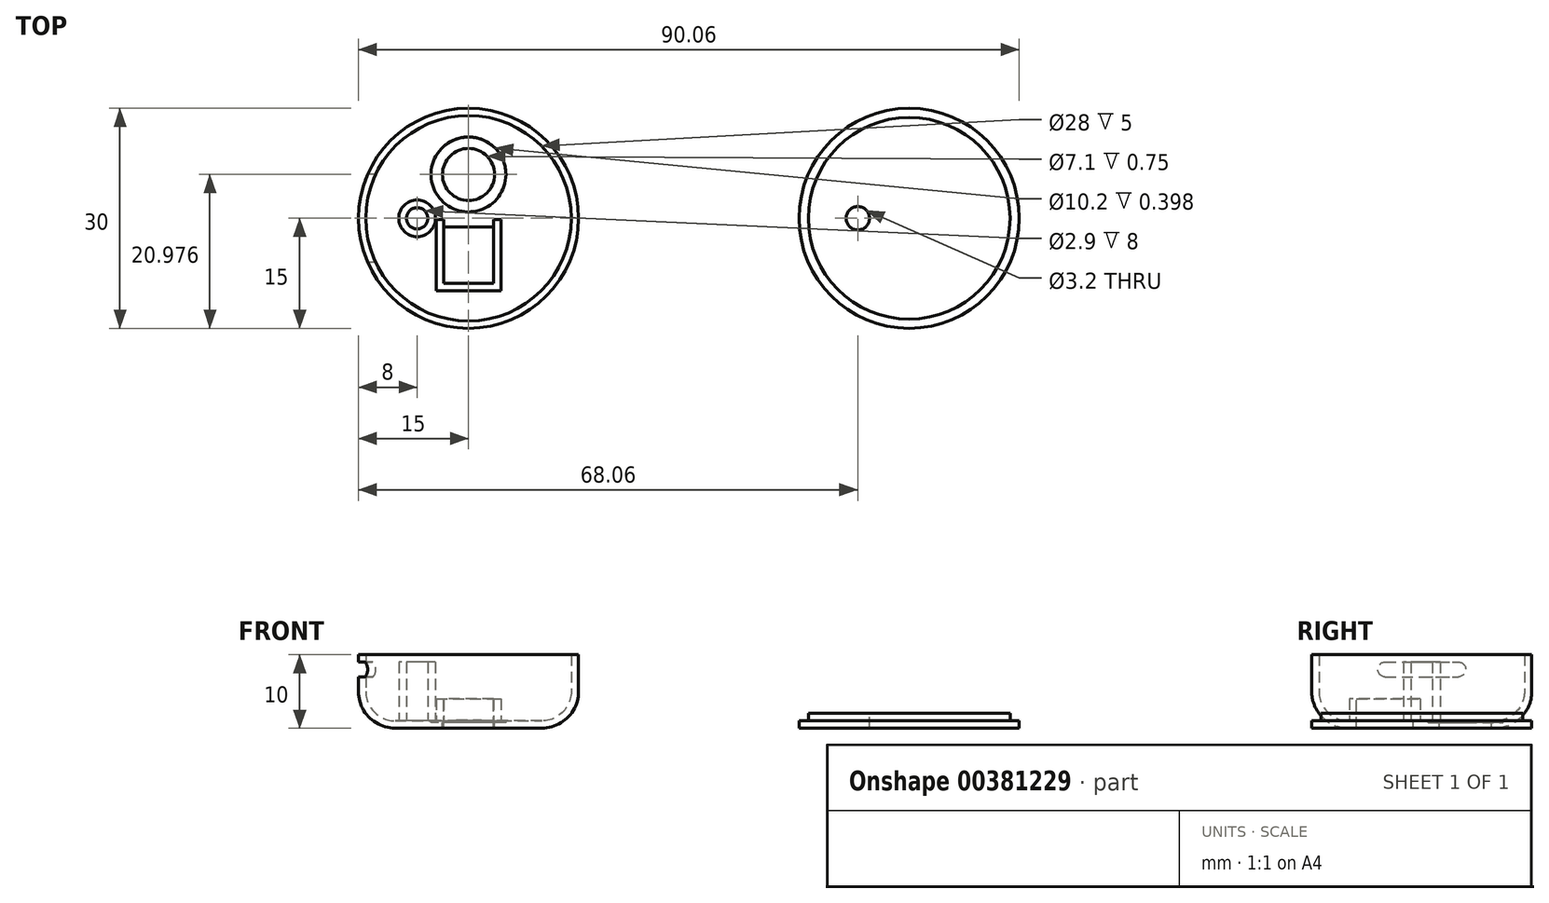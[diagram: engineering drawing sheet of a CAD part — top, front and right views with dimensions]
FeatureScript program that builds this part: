
annotation { "Feature Type Name" : "Feature", "Feature Type Description" : "" }
export const myFeature = defineFeature(function(context is Context, id is Id, definition is map)
    precondition{}
    {
        {
            var Q0;
            Q0=qCreatedBy(makeId("Top.planeOp"),FACE);
            var sketch = newSketch(context, id + "F0", { "sketchPlane" : qUnion([Q0])});
            skCircle(sketch, "E0", {"center": v(0, 0) * mm, "radius": 15 * mm});
            skLineSegment(sketch, "E1", {"start": v(0, 15) * mm, "end": v(0, -15) * mm, "construction": true});
            skSolve(sketch);
        }
        {
            var Q0;
            Q0=makeQuery(id+"F0.imprint","IMPRINT",FACE,{"disambiguationData":[TD([[makeQuery(id+"F0.imprint","IMPRINT",EDGE,{"derivedFrom":sQuery(id+"F0.wireOp",EDGE,"E0")}),1.0]])]});
            extrude(context, id + "F1", {"entities" : qUnion([Q0]), "depth" : 10 * mm});
        }
        {
            var Q0;
            Q0=makeQuery(id+"F1.opExtrude","CAP_EDGE",EDGE,{"disambiguationData":[OSD([sQuery(id+"F0.wireOp",EDGE,"E0")])],"isStart":true});
            fillet(context, id + "F2", {"entities" : qUnion([Q0]), "radius" : 5 * mm, "tangentPropagation" : true, "allowEdgeOverflow" : false});
        }
        {
            var Q0;
            Q0=makeQuery(id+"F1.opExtrude","CAP_FACE",FACE,{"disambiguationData":[OSD([sQuery(id+"F0.wireOp",EDGE,"E0")])],"isStart":false});
            shell(context, id + "F3", {"entities" : qUnion([Q0]), "thickness" : 1 * mm});
        }
        {
            var Q0;
            {var subQ0=sQuery(id+"F0.wireOp",EDGE,"E0");Q0=makeQuery(id+"F3.opShell","OFFSET_FACE",FACE,{"disambiguationData":[OSD([subQ0]),TDD([makeQuery(id+"F1.opExtrude","CAP_FACE",FACE,{"disambiguationData":[OSD([subQ0])],"isStart":true})])]});}
            var sketch = newSketch(context, id + "F4", { "sketchPlane" : qUnion([Q0])});
            skLineSegment(sketch, "E2", {"start": v(0, 10) * mm, "end": v(0, -10) * mm, "construction": true});
            skCircle(sketch, "E3", {"center": v(0, 5.98) * mm, "radius": 3.55 * mm});
            skCircle(sketch, "E4", {"center": v(0, 5.98) * mm, "radius": 5.1 * mm});
            skLineSegment(sketch, "E5.bottom", {"start": v(3.4, -1.17) * mm, "end": v(-3.4, -1.17) * mm});
            skLineSegment(sketch, "E5.top", {"start": v(3.4, -8.87) * mm, "end": v(-3.4, -8.87) * mm});
            skLineSegment(sketch, "E5.left", {"start": v(3.4, -1.17) * mm, "end": v(3.4, -8.87) * mm});
            skLineSegment(sketch, "E5.right", {"start": v(-3.4, -1.17) * mm, "end": v(-3.4, -8.87) * mm});
            skPoint(sketch, "E5.middle", {"position": v(0, -5.02) * mm});
            skLineSegment(sketch, "E6.bottom", {"start": v(-4.4, -0.17) * mm, "end": v(-3.4, -0.17) * mm});
            skLineSegment(sketch, "E6.top", {"start": v(-4.4, -9.87) * mm, "end": v(4.4, -9.87) * mm});
            skLineSegment(sketch, "E6.left", {"start": v(-4.4, -0.17) * mm, "end": v(-4.4, -9.87) * mm});
            skLineSegment(sketch, "E6.right", {"start": v(4.4, -0.17) * mm, "end": v(4.4, -9.87) * mm});
            skLineSegment(sketch, "E7", {"start": v(-3.4, -1.17) * mm, "end": v(-3.4, -0.17) * mm});
            skLineSegment(sketch, "E8", {"start": v(3.4, -1.17) * mm, "end": v(3.4, -0.17) * mm});
            skLineSegment(sketch, "E9.trimOffspring", {"start": v(3.4, -0.17) * mm, "end": v(4.4, -0.17) * mm});
            skSolve(sketch);
        }
        {
            var Q0;
            Q0=makeQuery(id+"F4.imprint","IMPRINT",FACE,{"disambiguationData":[TD([[makeQuery(id+"F4.imprint","IMPRINT",EDGE,{"derivedFrom":sQuery(id+"F4.wireOp",EDGE,"E5.bottom")}),1.0]])]});
            var Q1;
            Q1=makeQuery(id+"F4.imprint","IMPRINT",FACE,{"disambiguationData":[TD([[makeQuery(id+"F4.imprint","IMPRINT",EDGE,{"derivedFrom":sQuery(id+"F4.wireOp",EDGE,"E3")}),1.0]])]});
            extrude(context, id + "F5", {"entities" : qUnion([Q0, Q1]), "operationType" : NewBodyOperationType.REMOVE, "endBound" : BoundingType.UP_TO_NEXT, "oppositeDirection" : true, "depth" : 25 * mm});
        }
        {
            var Q0;
            Q0=makeQuery(id+"F4.imprint","IMPRINT",FACE,{"disambiguationData":[TD([[makeQuery(id+"F4.imprint","IMPRINT",EDGE,{"derivedFrom":sQuery(id+"F4.wireOp",EDGE,"E3")}),-1.0]])]});
            var Q1;
            {var subQ0=sQuery(id+"F4.wireOp",EDGE,"E4");var subQ1=sQuery(id+"F0.wireOp",EDGE,"E0");var subQ2=makeQuery(id+"F3.opShell","OFFSET_EDGE",EDGE,{"disambiguationData":[OSD([subQ1]),TDD([makeQuery(id+"F2.opFillet","BLEND_EDGE",EDGE,{"blendedFrom":[makeQuery(id+"F1.opExtrude","CAP_EDGE",EDGE,{"disambiguationData":[OSD([subQ1])],"isStart":true}),makeQuery(id+"F1.opExtrude","CAP_FACE",FACE,{"disambiguationData":[OSD([subQ1])],"isStart":true})],"blendedInto":[makeQuery(id+"F1.opExtrude","CAP_FACE",FACE,{"disambiguationData":[OSD([subQ1])],"isStart":true})]})])]});var subQ3=makeQuery(id+"F4.imprint","INTERSECT",VERTEX,{"disambiguationData":[OD(0.0)],"derivedFrom":[subQ2,subQ0]});Q1=makeQuery(id+"F4.imprint","IMPRINT",FACE,{"disambiguationData":[TD([[makeQuery(id+"F4.imprint","IMPRINT",EDGE,{"disambiguationData":[TD([[subQ3,1.0]])],"derivedFrom":subQ0}),1.0]])]});}
            extrude(context, id + "F6", {"entities" : qUnion([Q0, Q1]), "operationType" : NewBodyOperationType.REMOVE, "endBound" : BoundingType.SYMMETRIC, "oppositeDirection" : true, "depth" : .5 * mm});
        }
        {
            var Q0;
            Q0=makeQuery(id+"F4.imprint","IMPRINT",FACE,{"disambiguationData":[TD([[makeQuery(id+"F4.imprint","IMPRINT",EDGE,{"derivedFrom":sQuery(id+"F4.wireOp",EDGE,"E5.top")}),1.0]])]});
            var Q1;
            {var subQ0=sQuery(id+"F4.wireOp",EDGE,"E6.left");var subQ1=sQuery(id+"F4.wireOp",EDGE,"E6.top");var subQ2=makeQuery(id+"F4.imprint","INTERSECT",VERTEX,{"derivedFrom":[subQ1,subQ0]});Q1=makeQuery(id+"F4.imprint","IMPRINT",FACE,{"disambiguationData":[TD([[makeQuery(id+"F4.imprint","IMPRINT",EDGE,{"disambiguationData":[TD([[subQ2,-1.0]])],"derivedFrom":subQ1}),1.0]])]});}
            var Q2;
            {var subQ0=sQuery(id+"F4.wireOp",EDGE,"E6.right");var subQ1=sQuery(id+"F4.wireOp",EDGE,"E6.top");var subQ2=makeQuery(id+"F4.imprint","INTERSECT",VERTEX,{"derivedFrom":[subQ1,subQ0]});Q2=makeQuery(id+"F4.imprint","IMPRINT",FACE,{"disambiguationData":[TD([[makeQuery(id+"F4.imprint","IMPRINT",EDGE,{"disambiguationData":[TD([[subQ2,1.0]])],"derivedFrom":subQ1}),1.0]])]});}
            extrude(context, id + "F7", {"entities" : qUnion([Q0, Q1, Q2]), "operationType" : NewBodyOperationType.ADD, "depth" : 3 * mm});
        }
        {
            var Q0;
            {var subQ1=sQuery(id+"F0.wireOp",EDGE,"E0");Q0=makeQuery(id+"F7.boolean.opBoolean","SPLIT",FACE,{"disambiguationData":[TD([makeQuery(id+"F5.boolean.opBoolean","COPY",FACE,{"derivedFrom":makeQuery(id+"F5.opExtrude","SWEPT_FACE",FACE,{"disambiguationData":[OSD([sQuery(id+"F4.wireOp",EDGE,"E5.bottom")])]})})])],"derivedFrom":makeQuery(id+"F3.opShell","OFFSET_FACE",FACE,{"disambiguationData":[OSD([subQ1]),TDD([makeQuery(id+"F1.opExtrude","CAP_FACE",FACE,{"disambiguationData":[OSD([subQ1])],"isStart":true})])]})});}
            var sketch = newSketch(context, id + "F8", { "sketchPlane" : qUnion([Q0])});
            skCircle(sketch, "E10", {"center": v(-7, 0) * mm, "radius": 1.45 * mm});
            skCircle(sketch, "E11", {"center": v(-7, 0) * mm, "radius": 2.5 * mm});
            skSolve(sketch);
        }
        {
            var Q0;
            Q0=makeQuery(id+"F8.imprint","IMPRINT",FACE,{"disambiguationData":[TD([[makeQuery(id+"F8.imprint","IMPRINT",EDGE,{"derivedFrom":sQuery(id+"F8.wireOp",EDGE,"E10")}),-1.0]])]});
            extrude(context, id + "F9", {"entities" : qUnion([Q0]), "operationType" : NewBodyOperationType.ADD, "depth" : 8 * mm});
        }
        {
            var Q0;
            Q0=qCreatedBy(makeId("Right.planeOp"),FACE);
            cPlane(context, id + "F10", {"entities" : qUnion([Q0]), "cplaneType" : CPlaneType.OFFSET, "offset" : 15 * mm, "oppositeDirection" : true, "width" : 150 * mm, "height" : 150 * mm});
        }
        {
            var Q0;
            Q0=qCreatedBy(id+"F10.planeOp",FACE);
            var sketch = newSketch(context, id + "F11", { "sketchPlane" : qUnion([Q0])});
            skArc(sketch, "E12", {"start": v(5, 7) * mm, "mid": v(6, 8) * mm, "end": v(5, 9) * mm});
            skArc(sketch, "E13", {"start": v(-5, 9) * mm, "mid": v(-6, 8) * mm, "end": v(-5, 7) * mm});
            skLineSegment(sketch, "E14", {"start": v(5, 8) * mm, "end": v(-5, 8) * mm, "construction": true});
            skLineSegment(sketch, "E15", {"start": v(5, 9) * mm, "end": v(-5, 9) * mm});
            skLineSegment(sketch, "E16", {"start": v(5, 7) * mm, "end": v(-5, 7) * mm});
            skPoint(sketch, "E17", {"position": v(0, 8) * mm});
            skSolve(sketch);
        }
        {
            var Q0;
            Q0=makeQuery(id+"F11.imprint","IMPRINT",FACE,{"disambiguationData":[TD([[makeQuery(id+"F11.imprint","IMPRINT",EDGE,{"derivedFrom":sQuery(id+"F11.wireOp",EDGE,"E12")}),1.0]])]});
            var Q1;
            {var subQ0=sQuery(id+"F0.wireOp",EDGE,"E0");Q1=makeQuery(id+"F3.opShell","OFFSET_FACE",FACE,{"disambiguationData":[OSD([subQ0]),TDD([makeQuery(id+"F1.opExtrude","SWEPT_FACE",FACE,{"disambiguationData":[OSD([subQ0])]})])]});}
            extrude(context, id + "F12", {"entities" : qUnion([Q0]), "operationType" : NewBodyOperationType.REMOVE, "endBound" : BoundingType.UP_TO_SURFACE, "endBoundEntityFace" : qUnion([Q1]), "depth" : 25 * mm});
        }
        {
            var Q0;
            Q0=qCreatedBy(makeId("Top.planeOp"),FACE);
            var sketch = newSketch(context, id + "F13", { "sketchPlane" : qUnion([Q0])});
            skCircle(sketch, "E18", {"center": v(60.06, 0) * mm, "radius": 15 * mm});
            skCircle(sketch, "E19", {"center": v(60.06, 0) * mm, "radius": 13.75 * mm});
            skSolve(sketch);
        }
        {
            var Q0;
            Q0=makeQuery(id+"F13.imprint","IMPRINT",FACE,{"disambiguationData":[TD([[makeQuery(id+"F13.imprint","IMPRINT",EDGE,{"derivedFrom":sQuery(id+"F13.wireOp",EDGE,"E19")}),1.0]])]});
            extrude(context, id + "F14", {"entities" : qUnion([Q0]), "depth" : 2 * mm});
        }
        {
            var Q0;
            Q0=makeQuery(id+"F13.imprint","IMPRINT",FACE,{"disambiguationData":[TD([[makeQuery(id+"F13.imprint","IMPRINT",EDGE,{"derivedFrom":sQuery(id+"F13.wireOp",EDGE,"E18")}),1.0]])]});
            extrude(context, id + "F15", {"entities" : qUnion([Q0]), "operationType" : NewBodyOperationType.ADD, "depth" : 1 * mm});
        }
        {
            var Q0;
            Q0=makeQuery(id+"F14.opExtrude","CAP_FACE",FACE,{"disambiguationData":[OSD([sQuery(id+"F13.wireOp",EDGE,"E19")])],"isStart":false});
            var sketch = newSketch(context, id + "F16", { "sketchPlane" : qUnion([Q0])});
            skCircle(sketch, "E20", {"center": v(53.06, 0) * mm, "radius": 1.6 * mm});
            skSolve(sketch);
        }
        {
            var Q0;
            Q0=makeQuery(id+"F16.imprint","IMPRINT",FACE,{"disambiguationData":[TD([[makeQuery(id+"F16.imprint","IMPRINT",EDGE,{"derivedFrom":sQuery(id+"F16.wireOp",EDGE,"E20")}),1.0]])]});
            extrude(context, id + "F17", {"entities" : qUnion([Q0]), "operationType" : NewBodyOperationType.REMOVE, "endBound" : BoundingType.UP_TO_NEXT, "oppositeDirection" : true, "depth" : 25 * mm});
        }
    });
